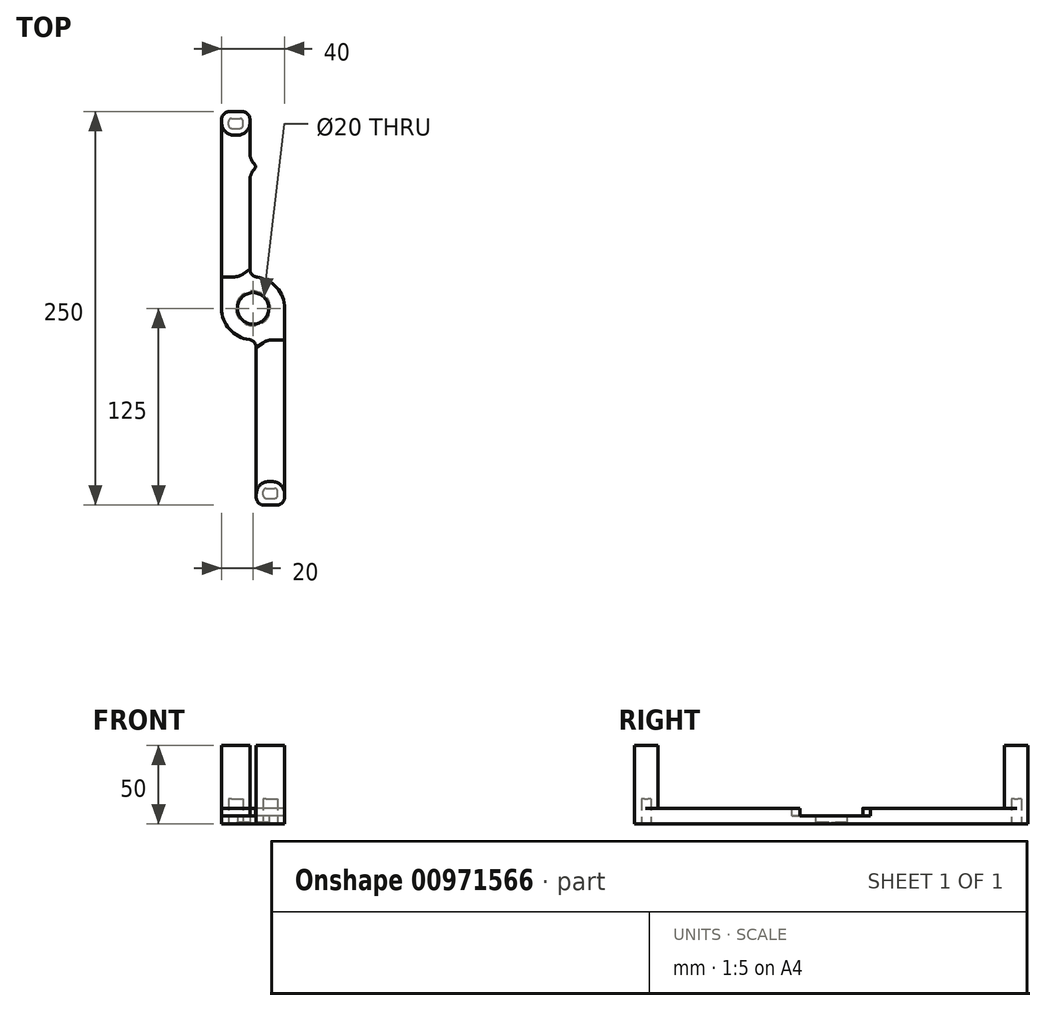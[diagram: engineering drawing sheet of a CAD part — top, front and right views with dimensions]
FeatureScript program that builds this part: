
annotation { "Feature Type Name" : "Feature", "Feature Type Description" : "" }
export const myFeature = defineFeature(function(context is Context, id is Id, definition is map)
    precondition{}
    {
        {
            var Q0;
            Q0=qCreatedBy(makeId("Top.planeOp"),FACE);
            var sketch = newSketch(context, id + "F0", { "sketchPlane" : qUnion([Q0])});
            skCircle(sketch, "E0", {"center": v(0, 0) * mm, "radius": 10 * mm});
            skArc(sketch, "E1", {"start": v(-20, 0) * mm, "mid": v(-14.97, -13.27) * mm, "end": v(-2.4, -19.86) * mm});
            skLineSegment(sketch, "E2", {"start": v(-20, 0) * mm, "end": v(-20, 120) * mm});
            skLineSegment(sketch, "E3", {"start": v(-2, 24.82) * mm, "end": v(-2, 81.5) * mm});
            skLineSegment(sketch, "E4", {"start": v(-7, 125) * mm, "end": v(-15, 125) * mm});
            skLineSegment(sketch, "E5", {"start": v(2, -24.82) * mm, "end": v(2, -120) * mm});
            skLineSegment(sketch, "E6", {"start": v(7, -125) * mm, "end": v(15, -125) * mm});
            skLineSegment(sketch, "E7", {"start": v(20, -120) * mm, "end": v(20, 0) * mm});
            skArc(sketch, "E8.trimOffspring", {"start": v(20, 0) * mm, "mid": v(14.97, 13.27) * mm, "end": v(2.4, 19.86) * mm});
            skLineSegment(sketch, "E9.trimOffspring", {"start": v(-2, 98.5) * mm, "end": v(-2, 120) * mm});
            skLineSegment(sketch, "E10", {"start": v(0.2, 92.26) * mm, "end": v(1.5, 90.62) * mm});
            skLineSegment(sketch, "E11", {"start": v(1.5, 89.38) * mm, "end": v(0.2, 87.74) * mm});
            skPoint(sketch, "E12.visualSharp", {"position": v(2, 90) * mm});
            skArc(sketch, "E12.filletArc", {"start": v(1.5, 89.38) * mm, "mid": v(1.72, 90) * mm, "end": v(1.5, 90.62) * mm});
            skPoint(sketch, "E13.visualSharp", {"position": v(-20, 125) * mm});
            skArc(sketch, "E13.filletArc", {"start": v(-15, 125) * mm, "mid": v(-18.54, 123.54) * mm, "end": v(-20, 120) * mm});
            skPoint(sketch, "E14.visualSharp", {"position": v(-2, 125) * mm});
            skArc(sketch, "E14.filletArc", {"start": v(-2, 120) * mm, "mid": v(-3.46, 123.54) * mm, "end": v(-7, 125) * mm});
            skPoint(sketch, "E15.visualSharp", {"position": v(2, -125) * mm});
            skArc(sketch, "E15.filletArc", {"start": v(2, -120) * mm, "mid": v(3.46, -123.54) * mm, "end": v(7, -125) * mm});
            skPoint(sketch, "E16.visualSharp", {"position": v(20, -125) * mm});
            skArc(sketch, "E16.filletArc", {"start": v(15, -125) * mm, "mid": v(18.54, -123.54) * mm, "end": v(20, -120) * mm});
            skPoint(sketch, "E17.visualSharp", {"position": v(-2, 85) * mm});
            skArc(sketch, "E17.filletArc", {"start": v(0.2, 87.74) * mm, "mid": v(-1.44, 84.8) * mm, "end": v(-2, 81.5) * mm});
            skPoint(sketch, "E18.visualSharp", {"position": v(-2, 95) * mm});
            skArc(sketch, "E18.filletArc", {"start": v(-2, 98.5) * mm, "mid": v(-1.44, 95.2) * mm, "end": v(0.2, 92.26) * mm});
            skPoint(sketch, "E19.visualSharp", {"position": v(2, -19.9) * mm});
            skArc(sketch, "E19.filletArc", {"start": v(2, -24.82) * mm, "mid": v(0.74, -21.5) * mm, "end": v(-2.4, -19.86) * mm});
            skPoint(sketch, "E20.visualSharp", {"position": v(-2, 19.9) * mm});
            skArc(sketch, "E20.filletArc", {"start": v(-2, 24.82) * mm, "mid": v(-0.74, 21.5) * mm, "end": v(2.4, 19.86) * mm});
            skSolve(sketch);
        }
        {
            var Q0;
            Q0 = qSketchRegion(id + "F0", true);
            extrude(context, id + "F1", {"entities" : qUnion([Q0]), "depth" : 10 * mm, "offsetDistance" : 25 * mm});
        }
        {
            var Q0;
            Q0=makeQuery(id+"F1.opExtrude","CAP_FACE",FACE,{"disambiguationData":[OSD([sQuery(id+"F0.wireOp",EDGE,"E0"),sQuery(id+"F0.wireOp",EDGE,"E1"),sQuery(id+"F0.wireOp",EDGE,"E2"),sQuery(id+"F0.wireOp",EDGE,"E3"),sQuery(id+"F0.wireOp",EDGE,"E4"),sQuery(id+"F0.wireOp",EDGE,"E5"),sQuery(id+"F0.wireOp",EDGE,"E6"),sQuery(id+"F0.wireOp",EDGE,"E7"),sQuery(id+"F0.wireOp",EDGE,"E8.trimOffspring")])],"isStart":false});
            var sketch = newSketch(context, id + "F2", { "sketchPlane" : qUnion([Q0])});
            skLineSegment(sketch, "E21", {"start": v(20, -20) * mm, "end": v(12.2, -20) * mm});
            skLineSegment(sketch, "E22", {"start": v(6.4, -21.86) * mm, "end": v(2, -25) * mm});
            skLineSegment(sketch, "E23", {"start": v(2, -25) * mm, "end": v(-20, -25) * mm});
            skLineSegment(sketch, "E24", {"start": v(-20, 20) * mm, "end": v(-12.2, 20) * mm});
            skLineSegment(sketch, "E25", {"start": v(-6.4, 21.86) * mm, "end": v(-2, 25) * mm});
            skLineSegment(sketch, "E26", {"start": v(-2, 25) * mm, "end": v(20, 25) * mm});
            skLineSegment(sketch, "E27", {"start": v(20, 25) * mm, "end": v(20, -20) * mm});
            skLineSegment(sketch, "E28", {"start": v(-20, 20) * mm, "end": v(-20, -25) * mm});
            skPoint(sketch, "E29.visualSharp", {"position": v(-9, 20) * mm});
            skArc(sketch, "E29.filletArc", {"start": v(-12.2, 20) * mm, "mid": v(-9.15, 20.48) * mm, "end": v(-6.4, 21.86) * mm});
            skPoint(sketch, "E30.visualSharp", {"position": v(9, -20) * mm});
            skArc(sketch, "E30.filletArc", {"start": v(12.2, -20) * mm, "mid": v(9.15, -20.48) * mm, "end": v(6.4, -21.86) * mm});
            skSolve(sketch);
        }
        {
            var Q0;
            Q0 = qSketchRegion(id + "F2", true);
            extrude(context, id + "F3", {"entities" : qUnion([Q0]), "operationType" : NewBodyOperationType.REMOVE, "oppositeDirection" : true, "depth" : 5 * mm, "offsetDistance" : 25 * mm});
        }
        {
            var Q0;
            {var subQ0=sQuery(id+"F0.wireOp",EDGE,"E9.trimOffspring");var subQ1=sQuery(id+"F0.wireOp",EDGE,"E4");var subQ2=sQuery(id+"F0.wireOp",EDGE,"E3");var subQ3=sQuery(id+"F0.wireOp",EDGE,"E2");var subQ4=sQuery(id+"F0.wireOp",EDGE,"E10");var subQ5=sQuery(id+"F0.wireOp",EDGE,"E11");var subQ6=sQuery(id+"F0.wireOp",EDGE,"E12.filletArc");Q0=makeQuery(id+"F3.boolean.opBoolean","SPLIT",FACE,{"disambiguationData":[TD([makeQuery(id+"F1.opExtrude","SWEPT_FACE",FACE,{"disambiguationData":[OSD([subQ3])]})])],"derivedFrom":makeQuery(id+"F1.opExtrude","CAP_FACE",FACE,{"disambiguationData":[OSD([sQuery(id+"F0.wireOp",EDGE,"E0"),sQuery(id+"F0.wireOp",EDGE,"E1"),subQ3,subQ2,subQ1,sQuery(id+"F0.wireOp",EDGE,"E5"),sQuery(id+"F0.wireOp",EDGE,"E6"),sQuery(id+"F0.wireOp",EDGE,"E7"),sQuery(id+"F0.wireOp",EDGE,"E8.trimOffspring"),subQ0,subQ4,subQ5,subQ6])],"isStart":false})});}
            var sketch = newSketch(context, id + "F4", { "sketchPlane" : qUnion([Q0])});
            skLineSegment(sketch, "E31.bottom", {"start": v(-15, 125) * mm, "end": v(-7, 125) * mm});
            skLineSegment(sketch, "E31.top", {"start": v(-12, 110) * mm, "end": v(-10, 110) * mm});
            skLineSegment(sketch, "E31.left", {"start": v(-20, 120) * mm, "end": v(-20, 118) * mm});
            skLineSegment(sketch, "E31.right", {"start": v(-2, 120) * mm, "end": v(-2, 118) * mm});
            skPoint(sketch, "E32.visualSharp", {"position": v(-20, 125) * mm});
            skArc(sketch, "E32.filletArc", {"start": v(-15, 125) * mm, "mid": v(-18.54, 123.54) * mm, "end": v(-20, 120) * mm});
            skPoint(sketch, "E33.visualSharp", {"position": v(-2, 125) * mm});
            skArc(sketch, "E33.filletArc", {"start": v(-2, 120) * mm, "mid": v(-3.46, 123.54) * mm, "end": v(-7, 125) * mm});
            skPoint(sketch, "E34.visualSharp", {"position": v(-20, 110) * mm});
            skArc(sketch, "E34.filletArc", {"start": v(-20, 118) * mm, "mid": v(-17.66, 112.34) * mm, "end": v(-12, 110) * mm});
            skPoint(sketch, "E35.visualSharp", {"position": v(-2, 110) * mm});
            skArc(sketch, "E35.filletArc", {"start": v(-10, 110) * mm, "mid": v(-4.34, 112.34) * mm, "end": v(-2, 118) * mm});
            skLineSegment(sketch, "E36.bottom", {"start": v(15, -125) * mm, "end": v(7, -125) * mm});
            skLineSegment(sketch, "E36.top", {"start": v(12, -110) * mm, "end": v(10, -110) * mm});
            skLineSegment(sketch, "E36.left", {"start": v(20, -120) * mm, "end": v(20, -118) * mm});
            skLineSegment(sketch, "E36.right", {"start": v(2, -120) * mm, "end": v(2, -118) * mm});
            skPoint(sketch, "E37.visualSharp", {"position": v(20, -125) * mm});
            skArc(sketch, "E37.filletArc", {"start": v(15, -125) * mm, "mid": v(18.54, -123.54) * mm, "end": v(20, -120) * mm});
            skPoint(sketch, "E38.visualSharp", {"position": v(2, -125) * mm});
            skArc(sketch, "E38.filletArc", {"start": v(2, -120) * mm, "mid": v(3.46, -123.54) * mm, "end": v(7, -125) * mm});
            skPoint(sketch, "E39.visualSharp", {"position": v(20, -110) * mm});
            skArc(sketch, "E39.filletArc", {"start": v(20, -118) * mm, "mid": v(17.66, -112.34) * mm, "end": v(12, -110) * mm});
            skPoint(sketch, "E40.visualSharp", {"position": v(2, -110) * mm});
            skArc(sketch, "E40.filletArc", {"start": v(10, -110) * mm, "mid": v(4.34, -112.34) * mm, "end": v(2, -118) * mm});
            skSolve(sketch);
        }
        {
            var Q0;
            Q0 = qSketchRegion(id + "F4", true);
            extrude(context, id + "F5", {"entities" : qUnion([Q0]), "operationType" : NewBodyOperationType.ADD, "depth" : 40 * mm, "offsetDistance" : 25 * mm});
        }
        {
            var Q0;
            Q0=makeQuery(id+"F1.opExtrude","CAP_EDGE",EDGE,{"disambiguationData":[OSD([sQuery(id+"F0.wireOp",EDGE,"E0")])],"isStart":true});
            chamfer(context, id + "F6", {"entities" : qUnion([Q0]), "width" : 1 * mm, "tangentPropagation" : true});
        }
        {
            var Q0;
            Q0=makeQuery(id+"F1.opExtrude","CAP_FACE",FACE,{"disambiguationData":[OSD([sQuery(id+"F0.wireOp",EDGE,"E0"),sQuery(id+"F0.wireOp",EDGE,"E1"),sQuery(id+"F0.wireOp",EDGE,"E2"),sQuery(id+"F0.wireOp",EDGE,"E3"),sQuery(id+"F0.wireOp",EDGE,"E4"),sQuery(id+"F0.wireOp",EDGE,"E5"),sQuery(id+"F0.wireOp",EDGE,"E6"),sQuery(id+"F0.wireOp",EDGE,"E7"),sQuery(id+"F0.wireOp",EDGE,"E8.trimOffspring"),sQuery(id+"F0.wireOp",EDGE,"E9.trimOffspring"),sQuery(id+"F0.wireOp",EDGE,"E10"),sQuery(id+"F0.wireOp",EDGE,"E11"),sQuery(id+"F0.wireOp",EDGE,"E12.filletArc"),sQuery(id+"F0.wireOp",EDGE,"E13.filletArc"),sQuery(id+"F0.wireOp",EDGE,"E14.filletArc"),sQuery(id+"F0.wireOp",EDGE,"E15.filletArc"),sQuery(id+"F0.wireOp",EDGE,"E16.filletArc"),sQuery(id+"F0.wireOp",EDGE,"E17.filletArc"),sQuery(id+"F0.wireOp",EDGE,"E18.filletArc"),sQuery(id+"F0.wireOp",EDGE,"E19.filletArc"),sQuery(id+"F0.wireOp",EDGE,"E20.filletArc")])],"isStart":true});
            var sketch = newSketch(context, id + "F7", { "sketchPlane" : qUnion([Q0])});
            skLineSegment(sketch, "E41", {"start": v(11, 125) * mm, "end": v(11, 109.04) * mm, "construction": true});
            skLineSegment(sketch, "E42.bottom", {"start": v(8.35, 120.65) * mm, "end": v(13.65, 120.65) * mm});
            skLineSegment(sketch, "E42.top", {"start": v(8.35, 114.35) * mm, "end": v(13.65, 114.35) * mm});
            skLineSegment(sketch, "E42.left", {"start": v(6.35, 118.65) * mm, "end": v(6.35, 116.35) * mm});
            skLineSegment(sketch, "E42.right", {"start": v(15.65, 118.65) * mm, "end": v(15.65, 116.35) * mm});
            skLineSegment(sketch, "E43", {"start": v(6.35, 114.35) * mm, "end": v(15.65, 120.65) * mm, "construction": true});
            skPoint(sketch, "E44", {"position": v(11, 117.5) * mm});
            skLineSegment(sketch, "E45.bottom", {"start": v(2, 110) * mm, "end": v(20, 110) * mm, "construction": true});
            skLineSegment(sketch, "E45.top", {"start": v(2, 125) * mm, "end": v(20, 125) * mm, "construction": true});
            skLineSegment(sketch, "E45.left", {"start": v(2, 110) * mm, "end": v(2, 125) * mm, "construction": true});
            skLineSegment(sketch, "E45.right", {"start": v(20, 110) * mm, "end": v(20, 125) * mm, "construction": true});
            skPoint(sketch, "E46.visualSharp", {"position": v(15.65, 120.65) * mm});
            skArc(sketch, "E46.filletArc", {"start": v(15.65, 118.65) * mm, "mid": v(15.06, 120.06) * mm, "end": v(13.65, 120.65) * mm});
            skPoint(sketch, "E47.visualSharp", {"position": v(15.65, 114.35) * mm});
            skArc(sketch, "E47.filletArc", {"start": v(13.65, 114.35) * mm, "mid": v(15.06, 114.94) * mm, "end": v(15.65, 116.35) * mm});
            skPoint(sketch, "E48.visualSharp", {"position": v(6.35, 114.35) * mm});
            skArc(sketch, "E48.filletArc", {"start": v(6.35, 116.35) * mm, "mid": v(6.94, 114.94) * mm, "end": v(8.35, 114.35) * mm});
            skPoint(sketch, "E49.visualSharp", {"position": v(6.35, 120.65) * mm});
            skArc(sketch, "E49.filletArc", {"start": v(8.35, 120.65) * mm, "mid": v(6.94, 120.06) * mm, "end": v(6.35, 118.65) * mm});
            skLineSegment(sketch, "E50", {"start": v(-11, -110) * mm, "end": v(-11, -125) * mm, "construction": true});
            skLineSegment(sketch, "E51.bottom", {"start": v(-13.65, -114.35) * mm, "end": v(-8.35, -114.35) * mm});
            skLineSegment(sketch, "E51.top", {"start": v(-13.65, -120.65) * mm, "end": v(-8.35, -120.65) * mm});
            skLineSegment(sketch, "E51.left", {"start": v(-15.65, -116.35) * mm, "end": v(-15.65, -118.65) * mm});
            skLineSegment(sketch, "E51.right", {"start": v(-6.35, -116.35) * mm, "end": v(-6.35, -118.65) * mm});
            skLineSegment(sketch, "E52", {"start": v(-15.65, -120.65) * mm, "end": v(-6.35, -114.35) * mm, "construction": true});
            skPoint(sketch, "E53", {"position": v(-11, -117.5) * mm});
            skLineSegment(sketch, "E54.bottom", {"start": v(-20, -125) * mm, "end": v(-2, -125) * mm, "construction": true});
            skLineSegment(sketch, "E54.top", {"start": v(-20, -110) * mm, "end": v(-2, -110) * mm, "construction": true});
            skLineSegment(sketch, "E54.left", {"start": v(-20, -125) * mm, "end": v(-20, -110) * mm, "construction": true});
            skLineSegment(sketch, "E54.right", {"start": v(-2, -125) * mm, "end": v(-2, -110) * mm, "construction": true});
            skPoint(sketch, "E55.visualSharp", {"position": v(-6.35, -114.35) * mm});
            skArc(sketch, "E55.filletArc", {"start": v(-6.35, -116.35) * mm, "mid": v(-6.94, -114.94) * mm, "end": v(-8.35, -114.35) * mm});
            skPoint(sketch, "E56.visualSharp", {"position": v(-6.35, -120.65) * mm});
            skArc(sketch, "E56.filletArc", {"start": v(-8.35, -120.65) * mm, "mid": v(-6.94, -120.06) * mm, "end": v(-6.35, -118.65) * mm});
            skPoint(sketch, "E57.visualSharp", {"position": v(-15.65, -120.65) * mm});
            skArc(sketch, "E57.filletArc", {"start": v(-15.65, -118.65) * mm, "mid": v(-15.06, -120.06) * mm, "end": v(-13.65, -120.65) * mm});
            skPoint(sketch, "E58.visualSharp", {"position": v(-15.65, -114.35) * mm});
            skArc(sketch, "E58.filletArc", {"start": v(-13.65, -114.35) * mm, "mid": v(-15.06, -114.94) * mm, "end": v(-15.65, -116.35) * mm});
            skSolve(sketch);
        }
        {
            var Q0;
            Q0 = qSketchRegion(id + "F7", true);
            extrude(context, id + "F8", {"entities" : qUnion([Q0]), "operationType" : NewBodyOperationType.REMOVE, "oppositeDirection" : true, "depth" : 16 * mm, "offsetDistance" : 25 * mm});
        }
    });
